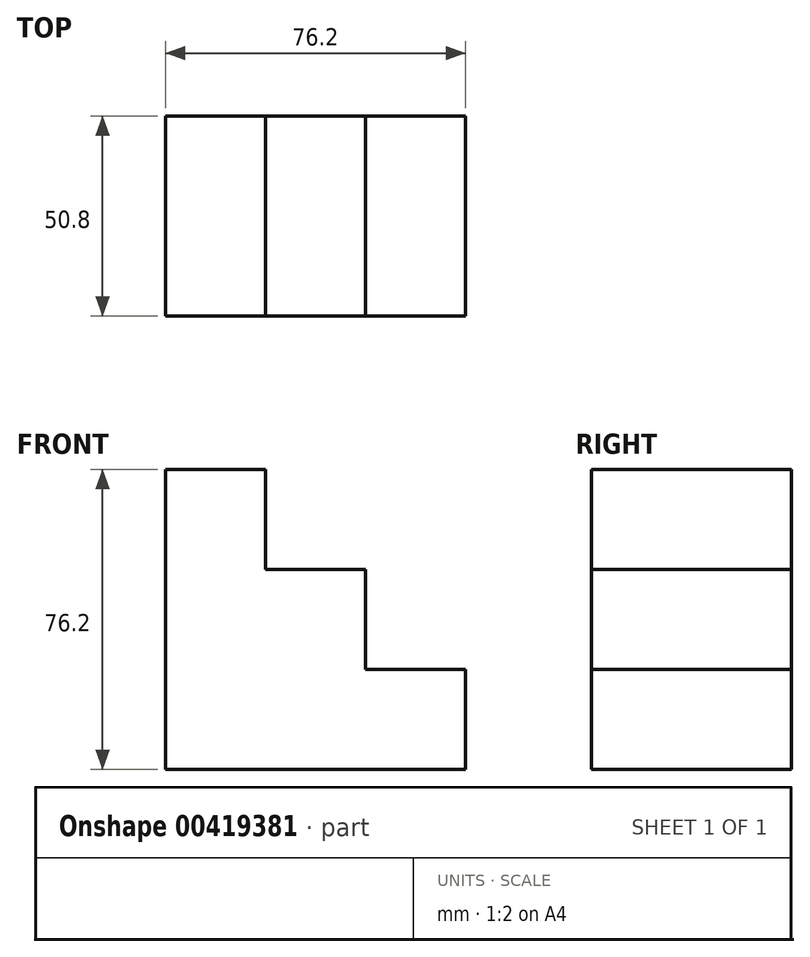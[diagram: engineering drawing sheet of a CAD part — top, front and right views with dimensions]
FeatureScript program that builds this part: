
annotation { "Feature Type Name" : "Feature", "Feature Type Description" : "" }
export const myFeature = defineFeature(function(context is Context, id is Id, definition is map)
    precondition{}
    {
        {
            var Q0;
            Q0=qCreatedBy(makeId("Front.planeOp"),FACE);
            var sketch = newSketch(context, id + "F0", { "sketchPlane" : qUnion([Q0])});
            skLineSegment(sketch, "E0", {"start": v(0, 0) * mm, "end": v(0, 76.2) * mm});
            skLineSegment(sketch, "E1", {"start": v(0, 0) * mm, "end": v(76.2, 0) * mm});
            skLineSegment(sketch, "E2", {"start": v(0, 76.2) * mm, "end": v(25.4, 76.2) * mm});
            skLineSegment(sketch, "E3", {"start": v(25.4, 76.2) * mm, "end": v(25.4, 50.8) * mm});
            skLineSegment(sketch, "E4", {"start": v(25.4, 50.8) * mm, "end": v(50.8, 50.8) * mm});
            skLineSegment(sketch, "E5", {"start": v(50.8, 50.8) * mm, "end": v(50.8, 25.4) * mm});
            skLineSegment(sketch, "E6", {"start": v(50.8, 25.4) * mm, "end": v(76.2, 25.4) * mm});
            skLineSegment(sketch, "E7", {"start": v(76.2, 25.4) * mm, "end": v(76.2, 0) * mm});
            skSolve(sketch);
        }
        {
            var Q0;
            Q0 = qSketchRegion(id + "F0", true);
            extrude(context, id + "F1", {"entities" : qUnion([Q0]), "depth" : 50.8 * mm});
        }
    });
